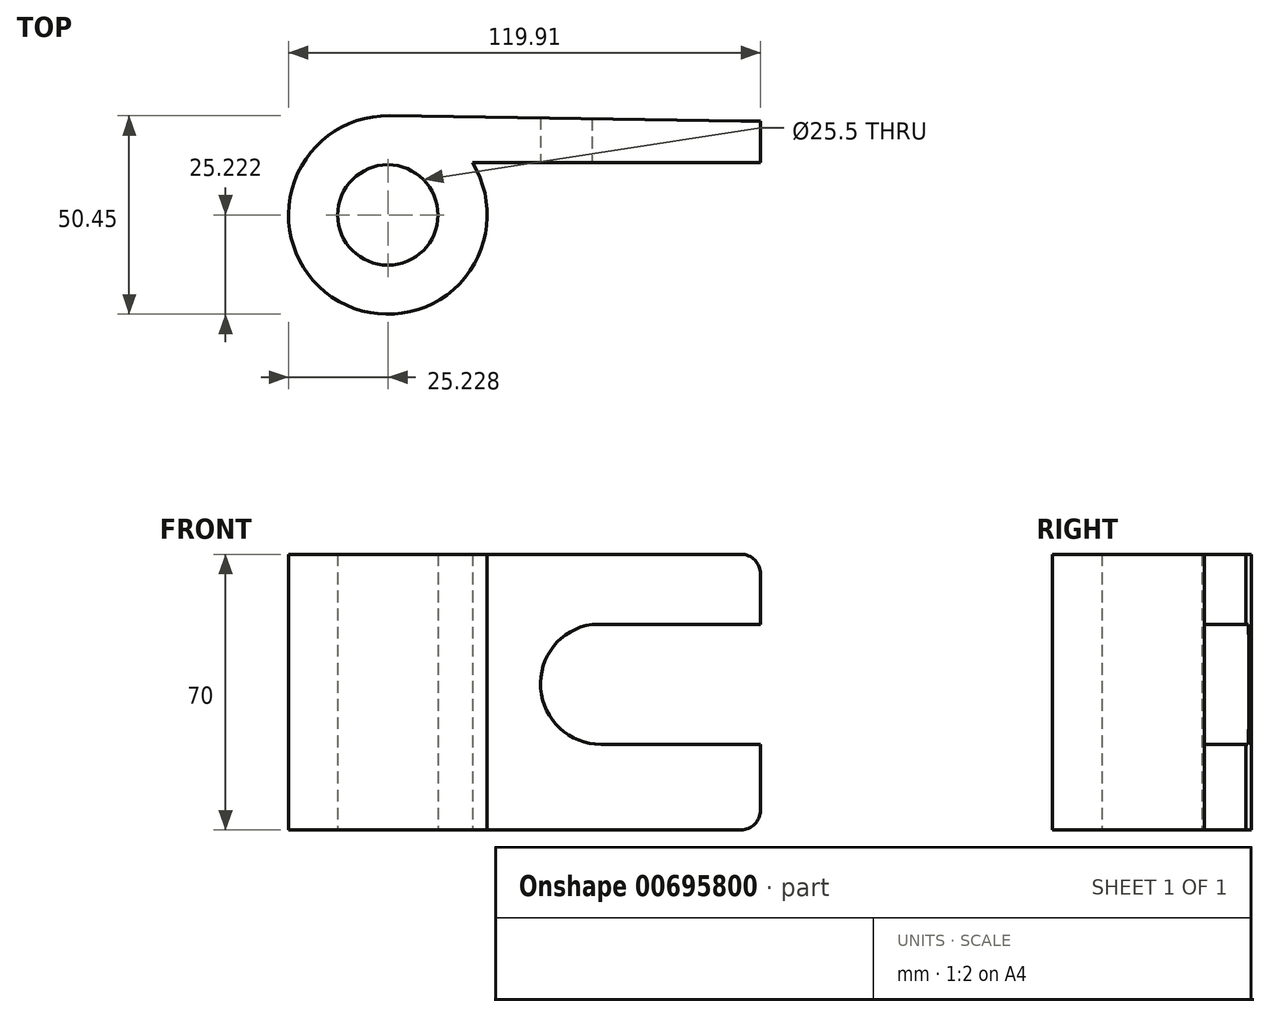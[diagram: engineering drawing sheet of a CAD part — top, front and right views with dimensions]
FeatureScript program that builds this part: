
annotation { "Feature Type Name" : "Feature", "Feature Type Description" : "" }
export const myFeature = defineFeature(function(context is Context, id is Id, definition is map)
    precondition{}
    {
        {
            var Q0;
            Q0=qCreatedBy(makeId("Top.planeOp"),FACE);
            var sketch = newSketch(context, id + "F0", { "sketchPlane" : qUnion([Q0])});
            skCircle(sketch, "E0", {"center": v(-45.04, 6.73) * mm, "radius": 25.22 * mm});
            skCircle(sketch, "E1", {"center": v(-45.04, 6.73) * mm, "radius": 12.75 * mm});
            skLineSegment(sketch, "E2", {"start": v(-44.67, 31.95) * mm, "end": v(49.64, 30.56) * mm});
            skLineSegment(sketch, "E3", {"start": v(49.64, 30.56) * mm, "end": v(49.64, 20) * mm});
            skLineSegment(sketch, "E4", {"start": v(49.64, 20) * mm, "end": v(-23.6, 20) * mm});
            skSolve(sketch);
        }
        {
            var Q0;
            Q0 = qSketchRegion(id + "F0", true);
            extrude(context, id + "F1", {"entities" : qUnion([Q0]), "depth" : 70 * mm, "offsetDistance" : 25 * mm});
        }
        {
            var Q0;
            Q0=makeQuery(id+"F1.opExtrude","SWEPT_FACE",FACE,{"disambiguationData":[OSD([sQuery(id+"F0.wireOp",EDGE,"E4")])]});
            var sketch = newSketch(context, id + "F2", { "sketchPlane" : qUnion([Q0])});
            skLineSegment(sketch, "E5", {"start": v(49.64, 52.24) * mm, "end": v(6.76, 52.24) * mm});
            skLineSegment(sketch, "E6", {"start": v(49.64, 21.73) * mm, "end": v(9.07, 21.73) * mm});
            skArc(sketch, "E7", {"start": v(6.76, 52.24) * mm, "mid": v(-6.23, 35.92) * mm, "end": v(9.07, 21.73) * mm});
            skSolve(sketch);
        }
        {
            var Q0;
            {var subQ0=sQuery(id+"F2.wireOp",EDGE,"E5");Q0=makeQuery(id+"F2.imprint","IMPRINT",FACE,{"disambiguationData":[TD([[makeQuery(id+"F2.imprint","IMPRINT",EDGE,{"derivedFrom":subQ0}),1.0]])]});}
            extrude(context, id + "F3", {"entities" : qUnion([Q0]), "operationType" : NewBodyOperationType.REMOVE, "oppositeDirection" : true, "depth" : 25 * mm, "offsetDistance" : 25 * mm});
        }
        {
            var Q0;
            Q0=makeQuery(id+"F1.opExtrude","CAP_EDGE",EDGE,{"disambiguationData":[OSD([sQuery(id+"F0.wireOp",EDGE,"E3")])],"isStart":false});
            var Q1;
            Q1=makeQuery(id+"F1.opExtrude","CAP_EDGE",EDGE,{"disambiguationData":[OSD([sQuery(id+"F0.wireOp",EDGE,"E3")])],"isStart":true});
            fillet(context, id + "F4", {"entities" : qUnion([Q0, Q1]), "radius" : 5 * mm, "tangentPropagation" : true, "allowEdgeOverflow" : false});
        }
    });
